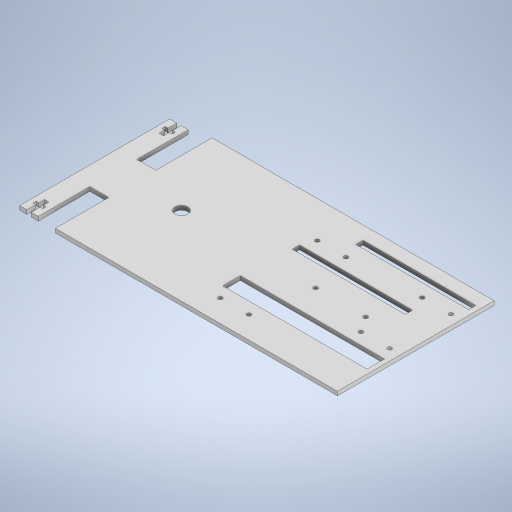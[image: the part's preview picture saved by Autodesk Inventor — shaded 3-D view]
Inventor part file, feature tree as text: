
AUTODESK INVENTOR PART (.ipt)
format: ipt  version: 2024 (Build 280153020, 153B)  size: 413,184 bytes
history: native  units: mm
features: extrude x7, sketch x6
ambient origin geometry x8: Origin, YZ Plane, XZ Plane, XY Plane, X Axis, Y Axis, Z Axis, Center Point
bodies: Solid1 (feature_tree)
feature tree (13):
  sketch  "Sketch1"  dims[d0=195.0mm d1=125.0mm]
  extrude  "Extrusion1"  Depth=125.0mm
  extrude  "Extrusion2"  Depth=40.0mm
  extrude  "Extrusion4"  Depth=41.0mm
  extrude  "Extrusion5"  Depth=3.25mm
  extrude  "Extrusion6"  Depth=1.5mm
  extrude  "Extrusion7"  Depth=3.25mm
  extrude  "Extrusion10"  Depth=3.25mm
  sketch  "Sketch2"  dims[d3=30.0mm d4=40.0mm]
  sketch  "Sketch3"  dims[d5=15.0mm d6=41.0mm]
  sketch  "Sketch4"  dims[d9=3.25mm d10=0.0mm d12=1.8mm]
  sketch  "Sketch5"  dims[d21=30.0mm d23=1.5mm]
  sketch  "Sketch8"  dims[d28=18.0mm d29=30.0mm d30=18.0mm d31=68.0mm d32=10.0mm d33=10.0mm d34=0.0mm d35=20.0mm d36=125.0mm d39=30.0mm d40=0.0mm d41=20.0mm d42=3.2mm d43=20.0mm d45=4.0mm d46=0.0mm d47=3.2mm d48=88.2mm d49=17.6mm d50=3.2mm d51=3.2mm d52=22.88mm d53=50.3mm d54=8.7mm d55=3.2mm d56=3.2mm d57=22.88mm d58=8.0mm d59=26.6mm d60=3.2mm d61=22.88mm d62=3.2mm d63=89.18mm d64=29.1mm d65=3.2mm d66=22.88mm d67=3.2mm d68=10.0mm d69=0.0mm d71=45.0mm d72=90.0mm d73=5.76mm d74=10.0mm d75=0.0mm d76=4.0mm d78=45.0mm d79=90.0mm d80=5.75mm d82=26.0mm d84=45.0mm d85=115.0mm d86=14.0mm d87=3.5mm d88=27.0mm d102=1.75mm d103=1.75mm d104=7.0mm d105=2.2mm d106=2.6mm d108=14.0mm d109=3.5mm d110=7.0mm d111=2.2mm d112=2.6mm d113=3.25mm d114=0.0mm]
